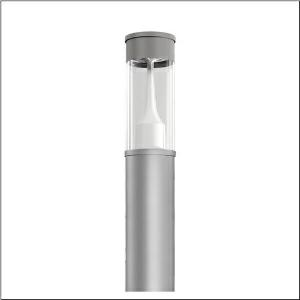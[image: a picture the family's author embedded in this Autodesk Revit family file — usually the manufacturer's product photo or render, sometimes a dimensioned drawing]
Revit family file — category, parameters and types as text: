
# Revit family: city-light_400_iq___p1_0a_5xa5305bf14hp_df67
name_source: partatom
category: Lighting Fixtures
units: mm (PartAtom-declared; Revit-internal decimal feet)

## family parameters
Cut with Voids When Loaded = No
Host = Face
Light Source = No
Part Type = Normal
Room Calculation Point = No
Round Connector Dimension = Use Diameter
Shared = No

## types (1)
- --- (1 x LED, 3890 lm, 33.6 W, 2200K)
    Apparent Load = 34 VA
    CIE Flux Codes = 31 62 91 95 100
    Color Rendering = 70
    Color Temperature = 2200K
    Default Elevation = 1800 mm
    Description = City-Light 400 iQ, light pillar, Module 540 iQ-SR, primary light control with 3 zone facetted reflector, of plastic, silver coated, highly specular, structured, primary optical cover: cover, of PMMA, transparent, partly coated, light distribution: P1.0a, primary light characteristic: strongly asymmetric, LED, High Power LED, rated luminous flux: 3.890lm, luminous efficacy: 116lm/W, light colour: 722, colour temperature: 2200K, control gear: ECG iQ, control: presetting dimming logarithmic, Street-Remote, Auto-Match, Temp-Guard, Lumen-Switch, Night-Set, Smart-Wire, Light-Fading, Desk-Remote (wireless, voltage-free reading and setting of iQ features in the workshop via application-optimized NFC function/RFID function), optimised constant luminous flux control (CLO 2.0), with terminal, 6-pole, max. 2.5mm², mains connection: 230..240V, AC, 50/60Hz, start of lifetime: 34W, end of service life: 36W, reduction: 15W, luminaire housing, cylindrical, of extruded aluminium section, coated, Siteco® metallic grey (DB 702S), length: 4.694mm, diameter: 200mm, Module 540 iQ-SR, traffic white (RAL 9016), equipment: Power, protection rating (complete): IP65, insulation class (complete): insulation class II (safety insulation), certification: CE, ENEC, VDE, packaging unit: 1 piece

Light Distribution: P1.0a
    Height = 500 mm
    Lamp = 1 x LED
    Lamp Light Flux = 3890 lm
    Lamp Power = 33.6 W
    Lamp count = 1
    Length = 200 mm  [stored 0.656168 ft]
    Luminous efficacy = 116 lm/W
    Manufacturer = Siteco
    ModVariant = No
    Model = 5XA5305BF14HP
    Mounting Place = Floor
    Mounting Type = Freestanding
    Number of Poles = 1
    OnlyDefault = Yes
    Power Factor = 1
    Product Name = City-Light 400 iQ | P1.0a
    Product group = light pillar
    ProductGroupID = 1303
    Protection Class = Protection class II
    Protection Degree = IP 65
    RLX_Detail_Level = 1
    RLX_Emergency_Light_Flux = 0 lm
    RLX_Emergency_Type = 0
    RLX_Emergency_Type_DB = No
    RlxData = <blob elided: 53433 chars, md5=4aee0380>
    Socket = socket
    Standby Power = 0 W
    System Light Flux = 3890 lm
    System Power = 34 W
    Type Comments = factory setting: luminous flux: 100 % | dim-lin: 254 | 695 mA
    Type Image = l_1006916.jpg
    URL = http://relux.com
    VarID = @adj_145429
    Voltage = 0 V
    Weight = 0.00 kg
    Width = 0 mm  [stored 0 ft]

note: [stored X ft] marks values corroborated as IEEE doubles in the binary element streams (Revit-internal decimal feet)

## geometry (parser evidence)
native form markers: Blend x4, Sweep x10
no freeform markers — native parametric forms only
